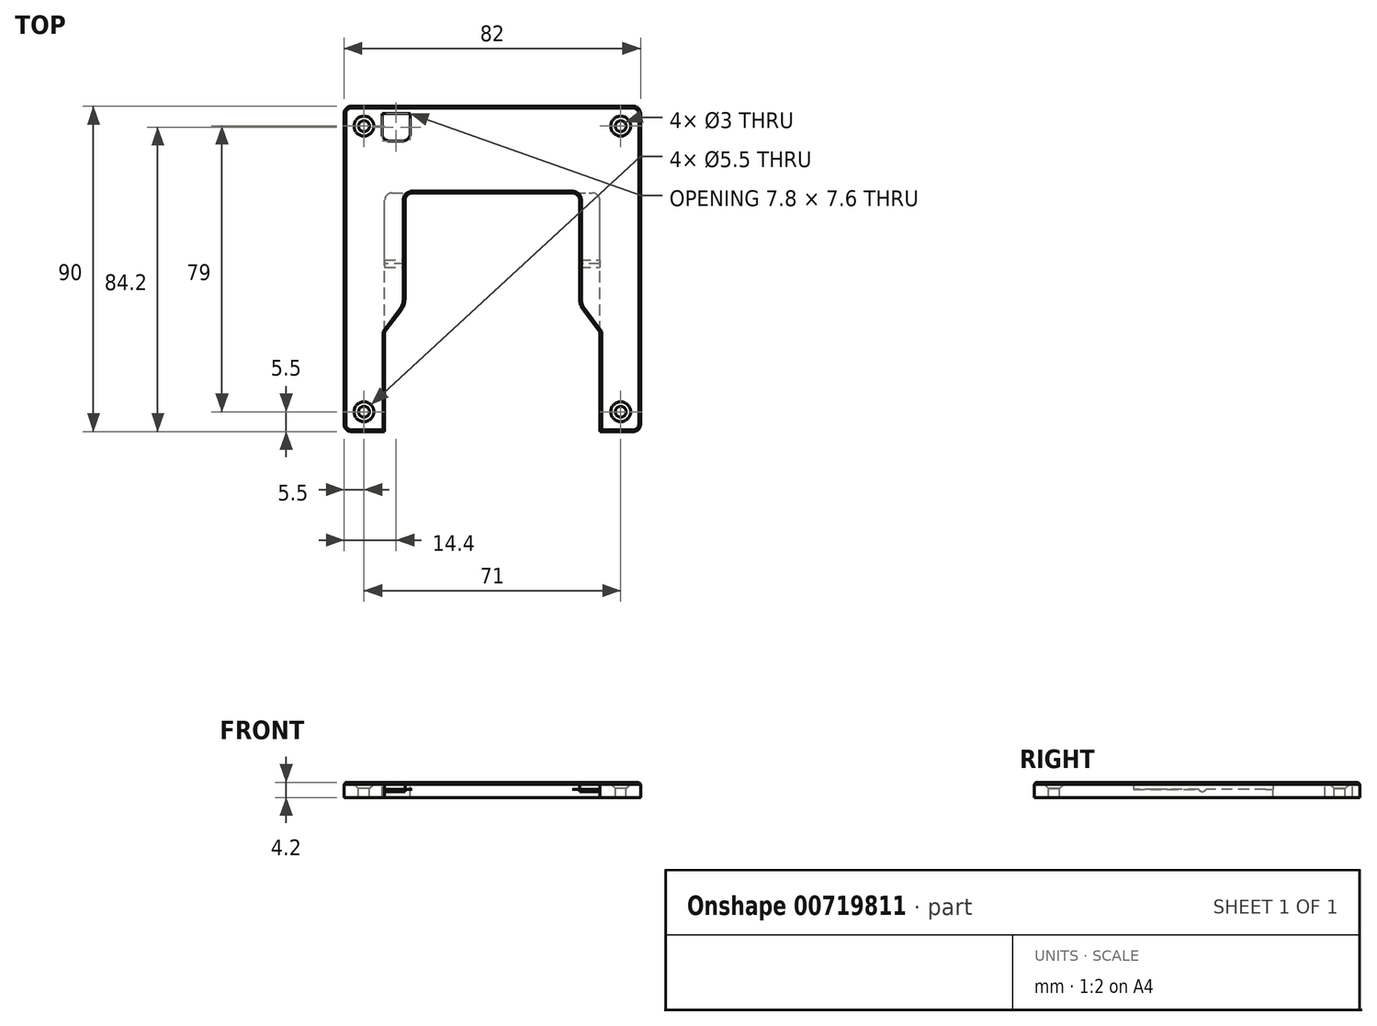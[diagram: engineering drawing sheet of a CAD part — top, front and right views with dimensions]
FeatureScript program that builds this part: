
annotation { "Feature Type Name" : "Feature", "Feature Type Description" : "" }
export const myFeature = defineFeature(function(context is Context, id is Id, definition is map)
    precondition{}
    {
        {
            var Q0;
            Q0=qCreatedBy(makeId("Top.planeOp"),FACE);
            var sketch = newSketch(context, id + "F0", { "sketchPlane" : qUnion([Q0])});
            skLineSegment(sketch, "E0.bottom", {"start": v(2, 0) * mm, "end": v(80, 0) * mm});
            skLineSegment(sketch, "E0.top", {"start": v(2, -90) * mm, "end": v(11.25, -90) * mm});
            skLineSegment(sketch, "E0.left", {"start": v(0, -2) * mm, "end": v(0, -88) * mm});
            skLineSegment(sketch, "E0.right", {"start": v(82, -2) * mm, "end": v(82, -88) * mm});
            skPoint(sketch, "E1.visualSharp", {"position": v(0, 0) * mm});
            skArc(sketch, "E1.filletArc", {"start": v(2, 0) * mm, "mid": v(0.59, -0.59) * mm, "end": v(0, -2) * mm});
            skPoint(sketch, "E2.visualSharp", {"position": v(82, 0) * mm});
            skArc(sketch, "E2.filletArc", {"start": v(82, -2) * mm, "mid": v(81.41, -0.59) * mm, "end": v(80, 0) * mm});
            skPoint(sketch, "E3.visualSharp", {"position": v(82, -90) * mm});
            skArc(sketch, "E3.filletArc", {"start": v(80, -90) * mm, "mid": v(81.41, -89.41) * mm, "end": v(82, -88) * mm});
            skPoint(sketch, "E4.visualSharp", {"position": v(0, -90) * mm});
            skArc(sketch, "E4.filletArc", {"start": v(0, -88) * mm, "mid": v(0.59, -89.41) * mm, "end": v(2, -90) * mm});
            skLineSegment(sketch, "E5.top", {"start": v(18.85, -24) * mm, "end": v(63.15, -24) * mm});
            skLineSegment(sketch, "E5.left", {"start": v(11.25, -90) * mm, "end": v(11.25, -62.5) * mm});
            skLineSegment(sketch, "E5.right", {"start": v(70.75, -90) * mm, "end": v(70.75, -62.5) * mm});
            skLineSegment(sketch, "E6.trimOffspring", {"start": v(70.75, -90) * mm, "end": v(80, -90) * mm});
            skLineSegment(sketch, "E7.right", {"start": v(16.85, -26) * mm, "end": v(16.85, -53.34) * mm});
            skLineSegment(sketch, "E8.right", {"start": v(65.15, -26) * mm, "end": v(65.15, -53.34) * mm});
            skPoint(sketch, "E9.visualSharp", {"position": v(16.85, -24) * mm});
            skArc(sketch, "E9.filletArc", {"start": v(18.85, -24) * mm, "mid": v(17.44, -24.59) * mm, "end": v(16.85, -26) * mm});
            skPoint(sketch, "E10.visualSharp", {"position": v(65.15, -24) * mm});
            skArc(sketch, "E10.filletArc", {"start": v(65.15, -26) * mm, "mid": v(64.56, -24.59) * mm, "end": v(63.15, -24) * mm});
            skPoint(sketch, "E11", {"position": v(16.85, -55) * mm});
            skLineSegment(sketch, "E12", {"start": v(11.25, -62.5) * mm, "end": v(15.86, -56.33) * mm});
            skLineSegment(sketch, "E13", {"start": v(66.14, -56.33) * mm, "end": v(70.75, -62.5) * mm});
            skArc(sketch, "E14.filletArc", {"start": v(15.86, -56.33) * mm, "mid": v(16.6, -54.92) * mm, "end": v(16.85, -53.34) * mm});
            skPoint(sketch, "E15.visualSharp", {"position": v(65.15, -55) * mm});
            skArc(sketch, "E15.filletArc", {"start": v(65.15, -53.34) * mm, "mid": v(65.4, -54.92) * mm, "end": v(66.14, -56.33) * mm});
            skSolve(sketch);
        }
        {
            var Q0;
            Q0=makeQuery(id+"F0.imprint","IMPRINT",FACE,{"disambiguationData":[TD([[makeQuery(id+"F0.imprint","IMPRINT",EDGE,{"derivedFrom":sQuery(id+"F0.wireOp",EDGE,"E0.bottom")}),-1.0]])]});
            extrude(context, id + "F1", {"entities" : qUnion([Q0]), "depth" : 2 * mm, "offsetDistance" : 25 * mm});
        }
        {
            var Q0;
            Q0=makeQuery(id+"F1.opExtrude","CAP_FACE",FACE,{"disambiguationData":[OSD([sQuery(id+"F0.wireOp",EDGE,"E0.bottom"),sQuery(id+"F0.wireOp",EDGE,"E0.top"),sQuery(id+"F0.wireOp",EDGE,"E0.left"),sQuery(id+"F0.wireOp",EDGE,"E0.right"),sQuery(id+"F0.wireOp",EDGE,"E1.filletArc"),sQuery(id+"F0.wireOp",EDGE,"E2.filletArc"),sQuery(id+"F0.wireOp",EDGE,"E3.filletArc"),sQuery(id+"F0.wireOp",EDGE,"E4.filletArc"),sQuery(id+"F0.wireOp",EDGE,"E5.top"),sQuery(id+"F0.wireOp",EDGE,"E5.left"),sQuery(id+"F0.wireOp",EDGE,"E5.right"),sQuery(id+"F0.wireOp",EDGE,"E6.trimOffspring"),sQuery(id+"F0.wireOp",EDGE,"E7.right"),sQuery(id+"F0.wireOp",EDGE,"E8.right"),sQuery(id+"F0.wireOp",EDGE,"E9.filletArc"),sQuery(id+"F0.wireOp",EDGE,"E10.filletArc"),sQuery(id+"F0.wireOp",EDGE,"E12"),sQuery(id+"F0.wireOp",EDGE,"E13"),sQuery(id+"F0.wireOp",EDGE,"E14.filletArc"),sQuery(id+"F0.wireOp",EDGE,"E15.filletArc")])],"isStart":true});
            var sketch = newSketch(context, id + "F2", { "sketchPlane" : qUnion([Q0])});
            skArc(sketch, "E16.0", {"start": v(82, 2) * mm, "mid": v(81.41, 0.59) * mm, "end": v(80, 0) * mm});
            skLineSegment(sketch, "E16.1", {"start": v(2, 0) * mm, "end": v(80, 0) * mm});
            skArc(sketch, "E16.2", {"start": v(2, 0) * mm, "mid": v(0.59, 0.59) * mm, "end": v(0, 2) * mm});
            skLineSegment(sketch, "E16.3", {"start": v(0, 2) * mm, "end": v(0, 88) * mm});
            skArc(sketch, "E16.4", {"start": v(0, 88) * mm, "mid": v(0.59, 89.41) * mm, "end": v(2, 90) * mm});
            skLineSegment(sketch, "E16.5", {"start": v(82, 2) * mm, "end": v(82, 88) * mm});
            skLineSegment(sketch, "E16.6", {"start": v(2, 90) * mm, "end": v(11.25, 90) * mm});
            skLineSegment(sketch, "E16.7", {"start": v(11.25, 90) * mm, "end": v(11.25, 62.5) * mm});
            skLineSegment(sketch, "E16.9", {"start": v(70.75, 90) * mm, "end": v(70.75, 62.5) * mm});
            skLineSegment(sketch, "E16.10", {"start": v(70.75, 90) * mm, "end": v(80, 90) * mm});
            skArc(sketch, "E16.11", {"start": v(80, 90) * mm, "mid": v(81.41, 89.41) * mm, "end": v(82, 88) * mm});
            skLineSegment(sketch, "E16.14", {"start": v(16.85, 24) * mm, "end": v(65.15, 24) * mm});
            skLineSegment(sketch, "E17", {"start": v(70.75, 62.5) * mm, "end": v(70.75, 26) * mm});
            skLineSegment(sketch, "E18", {"start": v(68.75, 24) * mm, "end": v(65.15, 24) * mm});
            skPoint(sketch, "E19.visualSharp", {"position": v(70.75, 24) * mm});
            skArc(sketch, "E19.filletArc", {"start": v(68.75, 24) * mm, "mid": v(70.16, 24.59) * mm, "end": v(70.75, 26) * mm});
            skLineSegment(sketch, "E20", {"start": v(11.25, 62.5) * mm, "end": v(11.25, 26) * mm});
            skLineSegment(sketch, "E21", {"start": v(13.25, 24) * mm, "end": v(16.85, 24) * mm});
            skPoint(sketch, "E22.visualSharp", {"position": v(11.25, 24) * mm});
            skArc(sketch, "E22.filletArc", {"start": v(11.25, 26) * mm, "mid": v(11.84, 24.59) * mm, "end": v(13.25, 24) * mm});
            skSolve(sketch);
        }
        {
            var Q0;
            Q0 = qSketchRegion(id + "F2", true);
            extrude(context, id + "F3", {"entities" : qUnion([Q0]), "operationType" : NewBodyOperationType.ADD, "depth" : 2.2 * mm, "offsetDistance" : 25 * mm});
        }
        {
            var Q0;
            Q0=makeQuery(id+"F1.opExtrude","CAP_FACE",FACE,{"disambiguationData":[OSD([sQuery(id+"F0.wireOp",EDGE,"E0.bottom"),sQuery(id+"F0.wireOp",EDGE,"E0.top"),sQuery(id+"F0.wireOp",EDGE,"E0.left"),sQuery(id+"F0.wireOp",EDGE,"E0.right"),sQuery(id+"F0.wireOp",EDGE,"E1.filletArc"),sQuery(id+"F0.wireOp",EDGE,"E2.filletArc"),sQuery(id+"F0.wireOp",EDGE,"E3.filletArc"),sQuery(id+"F0.wireOp",EDGE,"E4.filletArc"),sQuery(id+"F0.wireOp",EDGE,"E5.top"),sQuery(id+"F0.wireOp",EDGE,"E5.left"),sQuery(id+"F0.wireOp",EDGE,"E5.right"),sQuery(id+"F0.wireOp",EDGE,"E6.trimOffspring"),sQuery(id+"F0.wireOp",EDGE,"E7.right"),sQuery(id+"F0.wireOp",EDGE,"E8.right"),sQuery(id+"F0.wireOp",EDGE,"E9.filletArc"),sQuery(id+"F0.wireOp",EDGE,"E10.filletArc"),sQuery(id+"F0.wireOp",EDGE,"E12"),sQuery(id+"F0.wireOp",EDGE,"E13"),sQuery(id+"F0.wireOp",EDGE,"E14.filletArc"),sQuery(id+"F0.wireOp",EDGE,"E15.filletArc")])],"isStart":false});
            var sketch = newSketch(context, id + "F4", { "sketchPlane" : qUnion([Q0])});
            skLineSegment(sketch, "E23.bottom", {"start": v(10.5, -2) * mm, "end": v(18.3, -2) * mm});
            skLineSegment(sketch, "E23.top", {"start": v(12.5, -9.6) * mm, "end": v(16.3, -9.6) * mm});
            skLineSegment(sketch, "E23.left", {"start": v(10.5, -2) * mm, "end": v(10.5, -7.6) * mm});
            skLineSegment(sketch, "E23.right", {"start": v(18.3, -2) * mm, "end": v(18.3, -7.6) * mm});
            skPoint(sketch, "E24.visualSharp", {"position": v(10.5, -9.6) * mm});
            skArc(sketch, "E24.filletArc", {"start": v(10.5, -7.6) * mm, "mid": v(11.09, -9.01) * mm, "end": v(12.5, -9.6) * mm});
            skPoint(sketch, "E25.visualSharp", {"position": v(18.3, -9.6) * mm});
            skArc(sketch, "E25.filletArc", {"start": v(16.3, -9.6) * mm, "mid": v(17.71, -9.01) * mm, "end": v(18.3, -7.6) * mm});
            skSolve(sketch);
        }
        {
            var Q0;
            Q0 = qSketchRegion(id + "F4", true);
            extrude(context, id + "F5", {"entities" : qUnion([Q0]), "operationType" : NewBodyOperationType.REMOVE, "oppositeDirection" : true, "depth" : 25 * mm, "offsetDistance" : 25 * mm});
        }
        {
            var Q0;
            Q0=makeQuery(id+"F1.opExtrude","CAP_FACE",FACE,{"disambiguationData":[OSD([sQuery(id+"F0.wireOp",EDGE,"E0.bottom"),sQuery(id+"F0.wireOp",EDGE,"E0.top"),sQuery(id+"F0.wireOp",EDGE,"E0.left"),sQuery(id+"F0.wireOp",EDGE,"E0.right"),sQuery(id+"F0.wireOp",EDGE,"E1.filletArc"),sQuery(id+"F0.wireOp",EDGE,"E2.filletArc"),sQuery(id+"F0.wireOp",EDGE,"E3.filletArc"),sQuery(id+"F0.wireOp",EDGE,"E4.filletArc"),sQuery(id+"F0.wireOp",EDGE,"E5.top"),sQuery(id+"F0.wireOp",EDGE,"E5.left"),sQuery(id+"F0.wireOp",EDGE,"E5.right"),sQuery(id+"F0.wireOp",EDGE,"E6.trimOffspring"),sQuery(id+"F0.wireOp",EDGE,"E7.right"),sQuery(id+"F0.wireOp",EDGE,"E8.right"),sQuery(id+"F0.wireOp",EDGE,"E9.filletArc"),sQuery(id+"F0.wireOp",EDGE,"E10.filletArc"),sQuery(id+"F0.wireOp",EDGE,"E12"),sQuery(id+"F0.wireOp",EDGE,"E13"),sQuery(id+"F0.wireOp",EDGE,"E14.filletArc"),sQuery(id+"F0.wireOp",EDGE,"E15.filletArc")])],"isStart":false});
            var sketch = newSketch(context, id + "F6", { "sketchPlane" : qUnion([Q0])});
            skCircle(sketch, "E26", {"center": v(5.5, -5.5) * mm, "radius": 1.5 * mm});
            skCircle(sketch, "E27", {"center": v(76.5, -5.5) * mm, "radius": 1.5 * mm});
            skCircle(sketch, "E28", {"center": v(5.5, -84.5) * mm, "radius": 1.5 * mm});
            skCircle(sketch, "E29", {"center": v(76.5, -84.5) * mm, "radius": 1.5 * mm});
            skSolve(sketch);
        }
        {
            var Q0;
            Q0=makeQuery(id+"F6.imprint","IMPRINT",FACE,{"disambiguationData":[TD([[makeQuery(id+"F6.imprint","IMPRINT",EDGE,{"derivedFrom":sQuery(id+"F6.wireOp",EDGE,"E28")}),1.0]])]});
            var Q1;
            Q1=makeQuery(id+"F6.imprint","IMPRINT",FACE,{"disambiguationData":[TD([[makeQuery(id+"F6.imprint","IMPRINT",EDGE,{"derivedFrom":sQuery(id+"F6.wireOp",EDGE,"E29")}),1.0]])]});
            var Q2;
            Q2=makeQuery(id+"F6.imprint","IMPRINT",FACE,{"disambiguationData":[TD([[makeQuery(id+"F6.imprint","IMPRINT",EDGE,{"derivedFrom":sQuery(id+"F6.wireOp",EDGE,"E26")}),1.0]])]});
            var Q3;
            Q3=makeQuery(id+"F6.imprint","IMPRINT",FACE,{"disambiguationData":[TD([[makeQuery(id+"F6.imprint","IMPRINT",EDGE,{"derivedFrom":sQuery(id+"F6.wireOp",EDGE,"E27")}),1.0]])]});
            extrude(context, id + "F7", {"entities" : qUnion([Q0, Q1, Q2, Q3]), "operationType" : NewBodyOperationType.REMOVE, "oppositeDirection" : true, "depth" : 4.2 * mm, "offsetDistance" : 25 * mm});
        }
        {
            var Q0;
            Q0=makeQuery(id+"F1.opExtrude","CAP_FACE",FACE,{"disambiguationData":[OSD([sQuery(id+"F0.wireOp",EDGE,"E0.bottom"),sQuery(id+"F0.wireOp",EDGE,"E0.top"),sQuery(id+"F0.wireOp",EDGE,"E0.left"),sQuery(id+"F0.wireOp",EDGE,"E0.right"),sQuery(id+"F0.wireOp",EDGE,"E1.filletArc"),sQuery(id+"F0.wireOp",EDGE,"E2.filletArc"),sQuery(id+"F0.wireOp",EDGE,"E3.filletArc"),sQuery(id+"F0.wireOp",EDGE,"E4.filletArc"),sQuery(id+"F0.wireOp",EDGE,"E5.top"),sQuery(id+"F0.wireOp",EDGE,"E5.left"),sQuery(id+"F0.wireOp",EDGE,"E5.right"),sQuery(id+"F0.wireOp",EDGE,"E6.trimOffspring"),sQuery(id+"F0.wireOp",EDGE,"E7.right"),sQuery(id+"F0.wireOp",EDGE,"E8.right"),sQuery(id+"F0.wireOp",EDGE,"E9.filletArc"),sQuery(id+"F0.wireOp",EDGE,"E10.filletArc"),sQuery(id+"F0.wireOp",EDGE,"E12"),sQuery(id+"F0.wireOp",EDGE,"E13"),sQuery(id+"F0.wireOp",EDGE,"E14.filletArc"),sQuery(id+"F0.wireOp",EDGE,"E15.filletArc")])],"isStart":false});
            var sketch = newSketch(context, id + "F8", { "sketchPlane" : qUnion([Q0])});
            skCircle(sketch, "E30", {"center": v(5.5, -5.5) * mm, "radius": 2.75 * mm});
            skCircle(sketch, "E31", {"center": v(76.5, -5.5) * mm, "radius": 2.75 * mm});
            skCircle(sketch, "E32", {"center": v(76.5, -84.5) * mm, "radius": 2.75 * mm});
            skCircle(sketch, "E33", {"center": v(5.5, -84.5) * mm, "radius": 2.75 * mm});
            skSolve(sketch);
        }
        {
            var Q0;
            Q0 = qSketchRegion(id + "F8", true);
            extrude(context, id + "F9", {"entities" : qUnion([Q0]), "operationType" : NewBodyOperationType.REMOVE, "oppositeDirection" : true, "depth" : 2 * mm, "offsetDistance" : 25 * mm});
        }
        {
            var Q0;
            Q0=makeQuery(id+"F9.boolean.opBoolean","COPY",EDGE,{"derivedFrom":makeQuery(id+"F9.opExtrude","CAP_EDGE",EDGE,{"disambiguationData":[OSD([sQuery(id+"F8.wireOp",EDGE,"E33")])],"isStart":false})});
            var Q1;
            Q1=makeQuery(id+"F9.boolean.opBoolean","COPY",EDGE,{"derivedFrom":makeQuery(id+"F9.opExtrude","CAP_EDGE",EDGE,{"disambiguationData":[OSD([sQuery(id+"F8.wireOp",EDGE,"E32")])],"isStart":false})});
            var Q2;
            Q2=makeQuery(id+"F9.boolean.opBoolean","COPY",EDGE,{"derivedFrom":makeQuery(id+"F9.opExtrude","CAP_EDGE",EDGE,{"disambiguationData":[OSD([sQuery(id+"F8.wireOp",EDGE,"E30")])],"isStart":false})});
            var Q3;
            Q3=makeQuery(id+"F9.boolean.opBoolean","COPY",EDGE,{"derivedFrom":makeQuery(id+"F9.opExtrude","CAP_EDGE",EDGE,{"disambiguationData":[OSD([sQuery(id+"F8.wireOp",EDGE,"E31")])],"isStart":false})});
            chamfer(context, id + "F10", {"entities" : qUnion([Q0, Q1, Q2, Q3]), "width" : 1.5 * mm, "tangentPropagation" : true});
        }
        {
            var Q0;
            {var subQ0=sQuery(id+"F0.wireOp",EDGE,"E7.right");var subQ1=sQuery(id+"F0.wireOp",EDGE,"E9.filletArc");var subQ2=sQuery(id+"F0.wireOp",EDGE,"E5.left");var subQ3=sQuery(id+"F0.wireOp",EDGE,"E5.top");var subQ4=sQuery(id+"F0.wireOp",EDGE,"E12");var subQ5=sQuery(id+"F0.wireOp",EDGE,"E14.filletArc");Q0=makeQuery(id+"F3.boolean.opBoolean","SPLIT",FACE,{"disambiguationData":[TD([makeQuery(id+"F1.opExtrude","SWEPT_FACE",FACE,{"disambiguationData":[OSD([subQ2])]})])],"derivedFrom":makeQuery(id+"F1.opExtrude","CAP_FACE",FACE,{"disambiguationData":[OSD([sQuery(id+"F0.wireOp",EDGE,"E0.bottom"),sQuery(id+"F0.wireOp",EDGE,"E0.top"),sQuery(id+"F0.wireOp",EDGE,"E0.left"),sQuery(id+"F0.wireOp",EDGE,"E0.right"),sQuery(id+"F0.wireOp",EDGE,"E1.filletArc"),sQuery(id+"F0.wireOp",EDGE,"E2.filletArc"),sQuery(id+"F0.wireOp",EDGE,"E3.filletArc"),sQuery(id+"F0.wireOp",EDGE,"E4.filletArc"),subQ3,subQ2,sQuery(id+"F0.wireOp",EDGE,"E5.right"),sQuery(id+"F0.wireOp",EDGE,"E6.trimOffspring"),subQ0,sQuery(id+"F0.wireOp",EDGE,"E8.right"),subQ1,sQuery(id+"F0.wireOp",EDGE,"E10.filletArc"),subQ4,sQuery(id+"F0.wireOp",EDGE,"E13"),subQ5,sQuery(id+"F0.wireOp",EDGE,"E15.filletArc")])],"isStart":true})});}
            var sketch = newSketch(context, id + "F11", { "sketchPlane" : qUnion([Q0])});
            skLineSegment(sketch, "E34.bottom", {"start": v(11.25, 44.5) * mm, "end": v(16.85, 44.5) * mm});
            skLineSegment(sketch, "E34.top", {"start": v(11.25, 42.5) * mm, "end": v(16.85, 42.5) * mm});
            skLineSegment(sketch, "E34.left", {"start": v(11.25, 44.5) * mm, "end": v(11.25, 42.5) * mm});
            skLineSegment(sketch, "E34.right", {"start": v(16.85, 44.5) * mm, "end": v(16.85, 42.5) * mm});
            skLineSegment(sketch, "E35.bottom", {"start": v(65.15, 42.5) * mm, "end": v(70.75, 42.5) * mm});
            skLineSegment(sketch, "E35.top", {"start": v(65.15, 44.5) * mm, "end": v(70.75, 44.5) * mm});
            skLineSegment(sketch, "E35.left", {"start": v(65.15, 42.5) * mm, "end": v(65.15, 44.5) * mm});
            skLineSegment(sketch, "E35.right", {"start": v(70.75, 42.5) * mm, "end": v(70.75, 44.5) * mm});
            skSolve(sketch);
        }
        {
            var Q0;
            Q0 = qSketchRegion(id + "F11", true);
            extrude(context, id + "F12", {"entities" : qUnion([Q0]), "operationType" : NewBodyOperationType.ADD, "depth" : 0.6 * mm, "offsetDistance" : 25 * mm});
        }
        {
            var Q0;
            Q0=makeQuery(id+"F12.opExtrude","CAP_EDGE",EDGE,{"disambiguationData":[OSD([sQuery(id+"F11.wireOp",EDGE,"E34.top")])],"isStart":false});
            var Q1;
            Q1=makeQuery(id+"F12.opExtrude","CAP_EDGE",EDGE,{"disambiguationData":[OSD([sQuery(id+"F11.wireOp",EDGE,"E34.bottom")])],"isStart":false});
            var Q2;
            Q2=makeQuery(id+"F12.opExtrude","CAP_EDGE",EDGE,{"disambiguationData":[OSD([sQuery(id+"F11.wireOp",EDGE,"E35.bottom")])],"isStart":false});
            var Q3;
            Q3=makeQuery(id+"F12.opExtrude","CAP_EDGE",EDGE,{"disambiguationData":[OSD([sQuery(id+"F11.wireOp",EDGE,"E35.top")])],"isStart":false});
            fillet(context, id + "F13", {"entities" : qUnion([Q0, Q1, Q2, Q3]), "radius" : 1.4 * mm, "tangentPropagation" : true, "allowEdgeOverflow" : false});
        }
        {
            var Q0;
            Q0=makeQuery(id+"F1.opExtrude","CAP_EDGE",EDGE,{"disambiguationData":[OSD([sQuery(id+"F0.wireOp",EDGE,"E1.filletArc")])],"isStart":false});
            var Q1;
            Q1=makeQuery(id+"F1.opExtrude","CAP_EDGE",EDGE,{"disambiguationData":[OSD([sQuery(id+"F0.wireOp",EDGE,"E0.bottom")])],"isStart":false});
            var Q2;
            Q2=makeQuery(id+"F1.opExtrude","CAP_EDGE",EDGE,{"disambiguationData":[OSD([sQuery(id+"F0.wireOp",EDGE,"E0.left")])],"isStart":false});
            var Q3;
            Q3=makeQuery(id+"F5.boolean.opBoolean","COPY",EDGE,{"derivedFrom":makeQuery(id+"F5.opExtrude","CAP_EDGE",EDGE,{"disambiguationData":[OSD([sQuery(id+"F4.wireOp",EDGE,"E23.left")])],"isStart":true})});
            var Q4;
            Q4=makeQuery(id+"F5.boolean.opBoolean","COPY",EDGE,{"derivedFrom":makeQuery(id+"F5.opExtrude","CAP_EDGE",EDGE,{"disambiguationData":[OSD([sQuery(id+"F4.wireOp",EDGE,"E23.bottom")])],"isStart":true})});
            var Q5;
            Q5=makeQuery(id+"F5.boolean.opBoolean","COPY",EDGE,{"derivedFrom":makeQuery(id+"F5.opExtrude","CAP_EDGE",EDGE,{"disambiguationData":[OSD([sQuery(id+"F4.wireOp",EDGE,"E23.right")])],"isStart":true})});
            var Q6;
            Q6=makeQuery(id+"F5.boolean.opBoolean","COPY",EDGE,{"derivedFrom":makeQuery(id+"F5.opExtrude","CAP_EDGE",EDGE,{"disambiguationData":[OSD([sQuery(id+"F4.wireOp",EDGE,"E25.filletArc")])],"isStart":true})});
            var Q7;
            Q7=makeQuery(id+"F5.boolean.opBoolean","COPY",EDGE,{"derivedFrom":makeQuery(id+"F5.opExtrude","CAP_EDGE",EDGE,{"disambiguationData":[OSD([sQuery(id+"F4.wireOp",EDGE,"E23.top")])],"isStart":true})});
            var Q8;
            Q8=makeQuery(id+"F5.boolean.opBoolean","COPY",EDGE,{"derivedFrom":makeQuery(id+"F5.opExtrude","CAP_EDGE",EDGE,{"disambiguationData":[OSD([sQuery(id+"F4.wireOp",EDGE,"E24.filletArc")])],"isStart":true})});
            var Q9;
            Q9=makeQuery(id+"F1.opExtrude","CAP_EDGE",EDGE,{"disambiguationData":[OSD([sQuery(id+"F0.wireOp",EDGE,"E2.filletArc")])],"isStart":false});
            var Q10;
            Q10=makeQuery(id+"F1.opExtrude","CAP_EDGE",EDGE,{"disambiguationData":[OSD([sQuery(id+"F0.wireOp",EDGE,"E0.right")])],"isStart":false});
            var Q11;
            Q11=makeQuery(id+"F1.opExtrude","CAP_EDGE",EDGE,{"disambiguationData":[OSD([sQuery(id+"F0.wireOp",EDGE,"E5.left")])],"isStart":false});
            var Q12;
            Q12=makeQuery(id+"F1.opExtrude","CAP_EDGE",EDGE,{"disambiguationData":[OSD([sQuery(id+"F0.wireOp",EDGE,"E0.top")])],"isStart":false});
            var Q13;
            Q13=makeQuery(id+"F1.opExtrude","CAP_EDGE",EDGE,{"disambiguationData":[OSD([sQuery(id+"F0.wireOp",EDGE,"E4.filletArc")])],"isStart":false});
            var Q14;
            Q14=makeQuery(id+"F1.opExtrude","CAP_EDGE",EDGE,{"disambiguationData":[OSD([sQuery(id+"F0.wireOp",EDGE,"E3.filletArc")])],"isStart":false});
            var Q15;
            Q15=makeQuery(id+"F1.opExtrude","CAP_EDGE",EDGE,{"disambiguationData":[OSD([sQuery(id+"F0.wireOp",EDGE,"E6.trimOffspring")])],"isStart":false});
            var Q16;
            Q16=makeQuery(id+"F1.opExtrude","CAP_EDGE",EDGE,{"disambiguationData":[OSD([sQuery(id+"F0.wireOp",EDGE,"E5.right")])],"isStart":false});
            var Q17;
            Q17=makeQuery(id+"F1.opExtrude","CAP_EDGE",EDGE,{"disambiguationData":[OSD([sQuery(id+"F0.wireOp",EDGE,"E13")])],"isStart":false});
            var Q18;
            Q18=makeQuery(id+"F1.opExtrude","CAP_EDGE",EDGE,{"disambiguationData":[OSD([sQuery(id+"F0.wireOp",EDGE,"E15.filletArc")])],"isStart":false});
            var Q19;
            Q19=makeQuery(id+"F1.opExtrude","CAP_EDGE",EDGE,{"disambiguationData":[OSD([sQuery(id+"F0.wireOp",EDGE,"E8.right")])],"isStart":false});
            var Q20;
            Q20=makeQuery(id+"F1.opExtrude","CAP_EDGE",EDGE,{"disambiguationData":[OSD([sQuery(id+"F0.wireOp",EDGE,"E10.filletArc")])],"isStart":false});
            var Q21;
            Q21=makeQuery(id+"F1.opExtrude","CAP_EDGE",EDGE,{"disambiguationData":[OSD([sQuery(id+"F0.wireOp",EDGE,"E5.top")])],"isStart":false});
            var Q22;
            Q22=makeQuery(id+"F1.opExtrude","CAP_EDGE",EDGE,{"disambiguationData":[OSD([sQuery(id+"F0.wireOp",EDGE,"E9.filletArc")])],"isStart":false});
            var Q23;
            Q23=makeQuery(id+"F1.opExtrude","CAP_EDGE",EDGE,{"disambiguationData":[OSD([sQuery(id+"F0.wireOp",EDGE,"E7.right")])],"isStart":false});
            var Q24;
            Q24=makeQuery(id+"F1.opExtrude","CAP_EDGE",EDGE,{"disambiguationData":[OSD([sQuery(id+"F0.wireOp",EDGE,"E14.filletArc")])],"isStart":false});
            var Q25;
            Q25=makeQuery(id+"F1.opExtrude","CAP_EDGE",EDGE,{"disambiguationData":[OSD([sQuery(id+"F0.wireOp",EDGE,"E12")])],"isStart":false});
            chamfer(context, id + "F14", {"entities" : qUnion([Q0, Q1, Q2, Q3, Q4, Q5, Q6, Q7, Q8, Q9, Q10, Q11, Q12, Q13, Q14, Q15, Q16, Q17, Q18, Q19, Q20, Q21, Q22, Q23, Q24, Q25]), "width" : 0.5 * mm, "tangentPropagation" : true});
        }
    });
